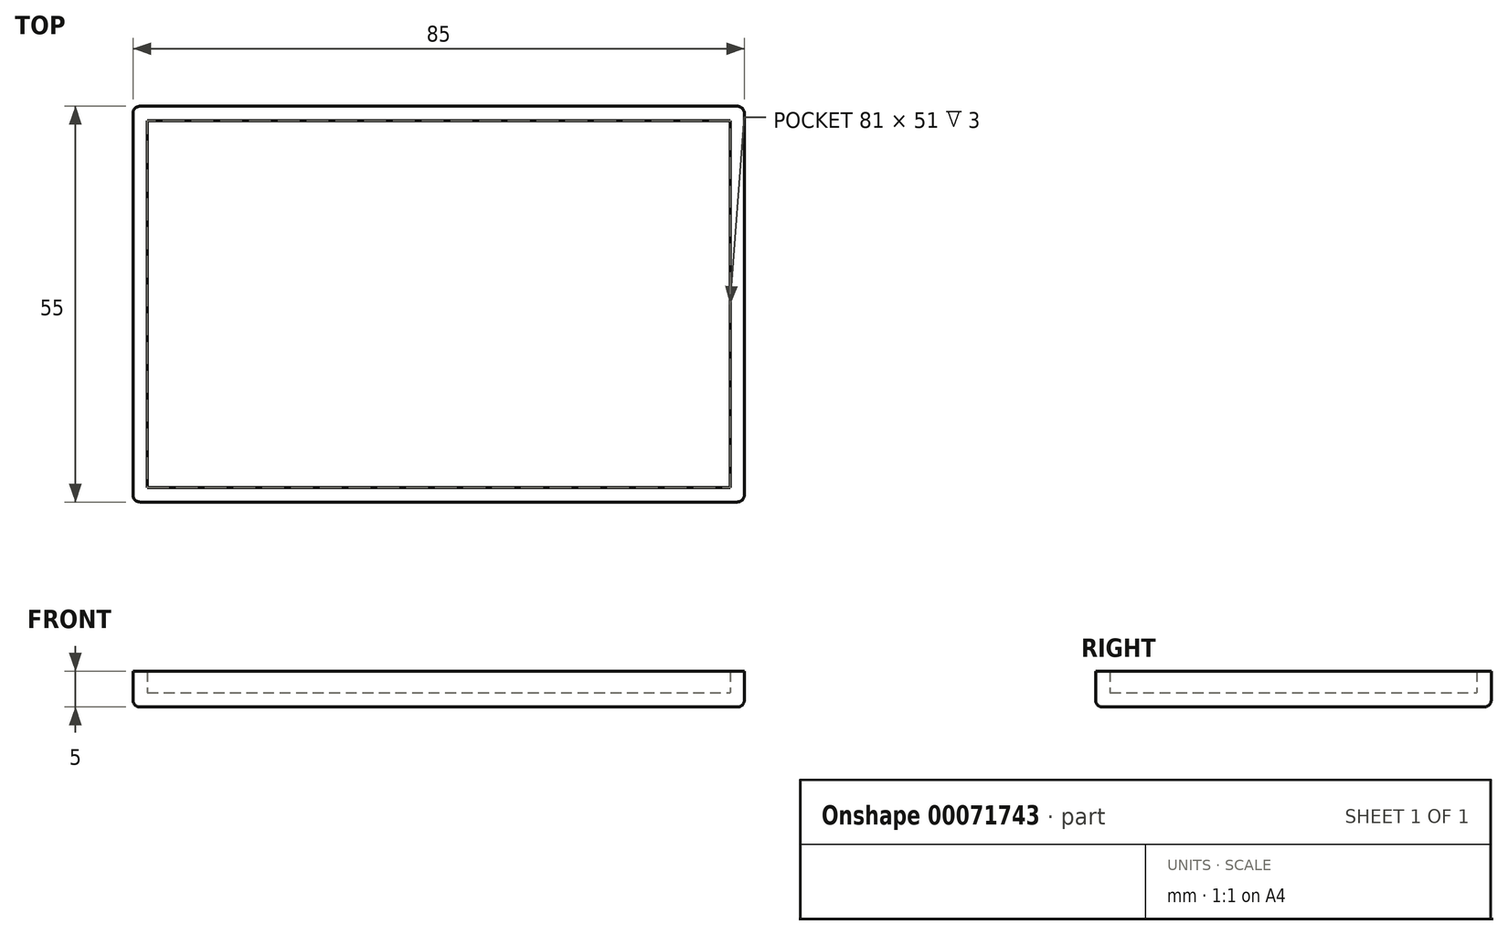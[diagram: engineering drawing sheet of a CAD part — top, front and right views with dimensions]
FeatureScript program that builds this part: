
annotation { "Feature Type Name" : "Feature", "Feature Type Description" : "" }
export const myFeature = defineFeature(function(context is Context, id is Id, definition is map)
    precondition{}
    {
        {
            var Q0;
            Q0=qCreatedBy(makeId("Top.planeOp"),FACE);
            var sketch = newSketch(context, id + "F0", { "sketchPlane" : qUnion([Q0])});
            skLineSegment(sketch, "E0.rect.bottom", {"start": v(-42.5, -27.5) * mm, "end": v(42.5, -27.5) * mm});
            skLineSegment(sketch, "E0.rect.top", {"start": v(-42.5, 27.5) * mm, "end": v(42.5, 27.5) * mm});
            skLineSegment(sketch, "E0.rect.left", {"start": v(-42.5, -27.5) * mm, "end": v(-42.5, 27.5) * mm});
            skLineSegment(sketch, "E0.rect.right", {"start": v(42.5, -27.5) * mm, "end": v(42.5, 27.5) * mm});
            skPoint(sketch, "E0.rect.middle", {"position": v(0, 0) * mm});
            skSolve(sketch);
        }
        {
            var Q0;
            Q0=makeQuery(id+"F0.imprint","IMPRINT",FACE,{"disambiguationData":[TD([[makeQuery(id+"F0.imprint","IMPRINT",EDGE,{"derivedFrom":sQuery(id+"F0.wireOp",EDGE,"E0.rect.bottom")}),1.0]])]});
            extrude(context, id + "F1", {"entities" : qUnion([Q0]), "depth" : 5 * mm});
        }
        {
            var Q0;
            Q0=makeQuery(id+"F1.opExtrude","CAP_FACE",FACE,{"disambiguationData":[OSD([sQuery(id+"F0.wireOp",EDGE,"E0.rect.bottom"),sQuery(id+"F0.wireOp",EDGE,"E0.rect.top"),sQuery(id+"F0.wireOp",EDGE,"E0.rect.left"),sQuery(id+"F0.wireOp",EDGE,"E0.rect.right")])],"isStart":false});
            shell(context, id + "F2", {"entities" : qUnion([Q0]), "thickness" : 2 * mm});
        }
        {
            var Q0;
            Q0=makeQuery(id+"F1.opExtrude","CAP_EDGE",EDGE,{"disambiguationData":[OSD([sQuery(id+"F0.wireOp",EDGE,"E0.rect.bottom")])],"isStart":true});
            fillet(context, id + "F3", {"entities" : qUnion([Q0]), "radius" : 1 * mm, "tangentPropagation" : true, "allowEdgeOverflow" : false});
        }
        {
            var Q0;
            Q0=makeQuery(id+"F1.opExtrude","CAP_EDGE",EDGE,{"disambiguationData":[OSD([sQuery(id+"F0.wireOp",EDGE,"E0.rect.left")])],"isStart":true});
            fillet(context, id + "F4", {"entities" : qUnion([Q0]), "radius" : 1 * mm, "tangentPropagation" : true, "allowEdgeOverflow" : false});
        }
        {
            var Q0;
            Q0=makeQuery(id+"F1.opExtrude","CAP_EDGE",EDGE,{"disambiguationData":[OSD([sQuery(id+"F0.wireOp",EDGE,"E0.rect.right")])],"isStart":true});
            fillet(context, id + "F5", {"entities" : qUnion([Q0]), "radius" : 1 * mm, "tangentPropagation" : true, "allowEdgeOverflow" : false});
        }
        {
            var Q0;
            Q0=makeQuery(id+"F1.opExtrude","CAP_EDGE",EDGE,{"disambiguationData":[OSD([sQuery(id+"F0.wireOp",EDGE,"E0.rect.top")])],"isStart":true});
            fillet(context, id + "F6", {"entities" : qUnion([Q0]), "radius" : 1 * mm, "tangentPropagation" : true, "allowEdgeOverflow" : false});
        }
    });
